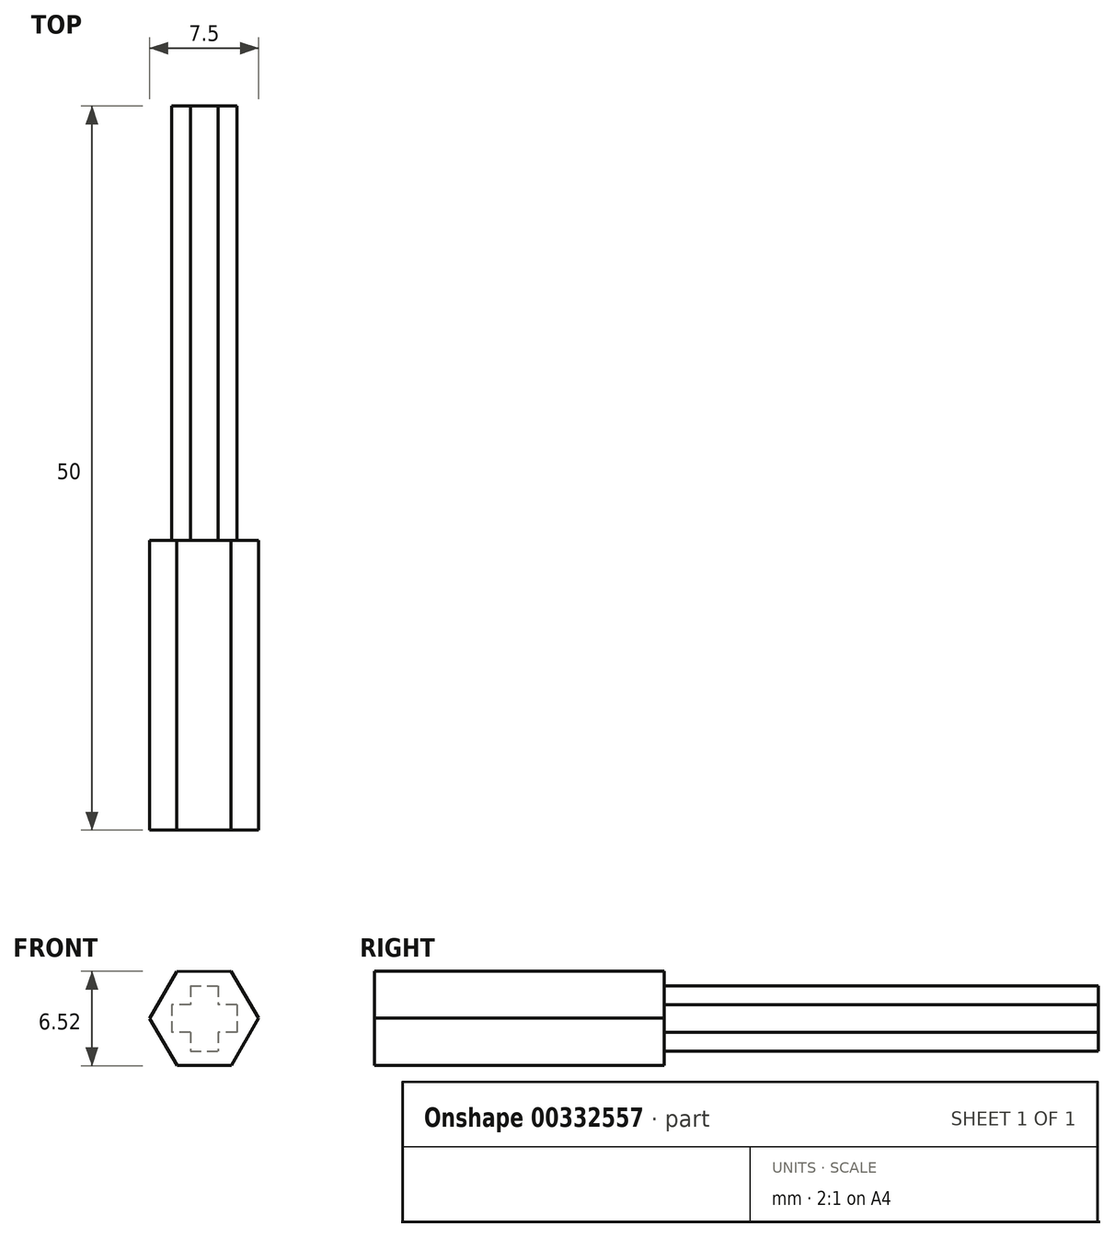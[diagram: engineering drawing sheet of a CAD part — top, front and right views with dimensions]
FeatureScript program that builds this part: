
annotation { "Feature Type Name" : "Feature", "Feature Type Description" : "" }
export const myFeature = defineFeature(function(context is Context, id is Id, definition is map)
    precondition{}
    {
        {
            var Q0;
            Q0=qCreatedBy(makeId("Front.planeOp"),FACE);
            var sketch = newSketch(context, id + "F0", { "sketchPlane" : qUnion([Q0])});
            skCircle(sketch, "E0.cCircle", {"center": v(0, 0) * mm, "radius": 3.25 * mm, "construction": true});
            skLineSegment(sketch, "E0.0", {"start": v(1.86, 3.26) * mm, "end": v(3.75, 0.02) * mm});
            skLineSegment(sketch, "E0.1", {"start": v(3.75, 0.02) * mm, "end": v(1.89, -3.24) * mm});
            skLineSegment(sketch, "E0.2", {"start": v(1.89, -3.24) * mm, "end": v(-1.86, -3.26) * mm});
            skLineSegment(sketch, "E0.3", {"start": v(-1.86, -3.26) * mm, "end": v(-3.75, -0.02) * mm});
            skLineSegment(sketch, "E0.4", {"start": v(-3.75, -0.02) * mm, "end": v(-1.89, 3.24) * mm});
            skLineSegment(sketch, "E0.5", {"start": v(-1.89, 3.24) * mm, "end": v(1.86, 3.26) * mm});
            skPoint(sketch, "E0.0.midPoint", {"position": v(2.8, 1.64) * mm});
            skSolve(sketch);
        }
        {
            var Q0;
            Q0=makeQuery(id+"F0.imprint","IMPRINT",FACE,{"disambiguationData":[TD([[makeQuery(id+"F0.imprint","IMPRINT",EDGE,{"derivedFrom":sQuery(id+"F0.wireOp",EDGE,"E0.0")}),-1.0]])]});
            extrude(context, id + "F1", {"entities" : qUnion([Q0]), "depth" : 20 * mm});
        }
        {
            var Q0;
            Q0=qCreatedBy(makeId("Front.planeOp"),FACE);
            var sketch = newSketch(context, id + "F2", { "sketchPlane" : qUnion([Q0])});
            skLineSegment(sketch, "E1.bottom", {"start": v(-0.95, 2.25) * mm, "end": v(0.95, 2.25) * mm});
            skLineSegment(sketch, "E1.top", {"start": v(-0.95, -2.25) * mm, "end": v(0.95, -2.25) * mm});
            skLineSegment(sketch, "E1.left", {"start": v(-0.95, 2.25) * mm, "end": v(-0.95, -2.25) * mm});
            skLineSegment(sketch, "E1.right", {"start": v(0.95, 2.25) * mm, "end": v(0.95, -2.25) * mm});
            skPoint(sketch, "E1.middle", {"position": v(0, 0) * mm});
            skLineSegment(sketch, "E2.bottom", {"start": v(2.25, 0.95) * mm, "end": v(-2.25, 0.95) * mm});
            skLineSegment(sketch, "E2.top", {"start": v(2.25, -0.95) * mm, "end": v(-2.25, -0.95) * mm});
            skLineSegment(sketch, "E2.left", {"start": v(2.25, 0.95) * mm, "end": v(2.25, -0.95) * mm});
            skLineSegment(sketch, "E2.right", {"start": v(-2.25, 0.95) * mm, "end": v(-2.25, -0.95) * mm});
            skSolve(sketch);
        }
        {
            var Q0;
            {var subQ0=sQuery(id+"F2.wireOp",EDGE,"E1.bottom");Q0=makeQuery(id+"F2.imprint","IMPRINT",FACE,{"disambiguationData":[TD([[makeQuery(id+"F2.imprint","IMPRINT",EDGE,{"derivedFrom":subQ0}),-1.0]])]});}
            var Q1;
            {var subQ5=sQuery(id+"F2.wireOp",EDGE,"E2.right");Q1=makeQuery(id+"F2.imprint","IMPRINT",FACE,{"disambiguationData":[TD([[makeQuery(id+"F2.imprint","IMPRINT",EDGE,{"derivedFrom":subQ5}),1.0]])]});}
            var Q2;
            {var subQ0=sQuery(id+"F2.wireOp",EDGE,"E2.bottom");var subQ1=sQuery(id+"F2.wireOp",EDGE,"E1.left");var subQ2=makeQuery(id+"F2.imprint","INTERSECT",VERTEX,{"derivedFrom":[subQ1,subQ0]});Q2=makeQuery(id+"F2.imprint","IMPRINT",FACE,{"disambiguationData":[TD([[makeQuery(id+"F2.imprint","IMPRINT",EDGE,{"disambiguationData":[TD([[subQ2,-1.0]])],"derivedFrom":subQ1}),1.0]])]});}
            var Q3;
            {var subQ5=sQuery(id+"F2.wireOp",EDGE,"E2.left");Q3=makeQuery(id+"F2.imprint","IMPRINT",FACE,{"disambiguationData":[TD([[makeQuery(id+"F2.imprint","IMPRINT",EDGE,{"derivedFrom":subQ5}),-1.0]])]});}
            var Q4;
            {var subQ0=sQuery(id+"F2.wireOp",EDGE,"E1.top");Q4=makeQuery(id+"F2.imprint","IMPRINT",FACE,{"disambiguationData":[TD([[makeQuery(id+"F2.imprint","IMPRINT",EDGE,{"derivedFrom":subQ0}),1.0]])]});}
            extrude(context, id + "F3", {"entities" : qUnion([Q0, Q1, Q2, Q3, Q4]), "operationType" : NewBodyOperationType.ADD, "oppositeDirection" : true, "depth" : 30 * mm});
        }
    });
